# Revit family: Boxer ks 178
name_source: partatom
category: Мебель
revit_build: Autodesk Revit 2017 (Build: 20160225_1515(x64)
units: mm (PartAtom-declared; Revit-internal decimal feet)

## family parameters
Всегда вертикально = Да
Заголовок OmniClass = General Furniture and Specialties
На основе рабочей плоскости = Нет
Номер OmniClass = 23.40.20.00
Общий = Нет
При загрузке вырезать с полостями = Нет
Точка расчета площади = Нет

## types (4) — shared parameters
Bench = Skandiform Fabric
Leg = Skandiform Chrome
Изготовитель = Skandiform AB
Комментарии к типоразмеру = Created by Astacus AB
Описание = Sofa. Base in chrome or silver painted metal

## per-type parameters (varying)
| type | Type | URL | Группа модели | Ключевая пометка |
| F-288 | KS-178 | http://file-system.ru | F288 | XBF.3 |
| KS-178 | KS-178 | http://www.biminfo.se | KS-178 | XBF.3 |
| SA-289 | SA-289 | http://www.biminfo.se | SA-289 | XBF.4 |
| SA-290 | SA-290 | http://www.biminfo.se | SA-290 | XBF.4 |

## geometry (parser evidence)
native form markers: Blend x6, Sweep x12
no freeform markers — native parametric forms only
